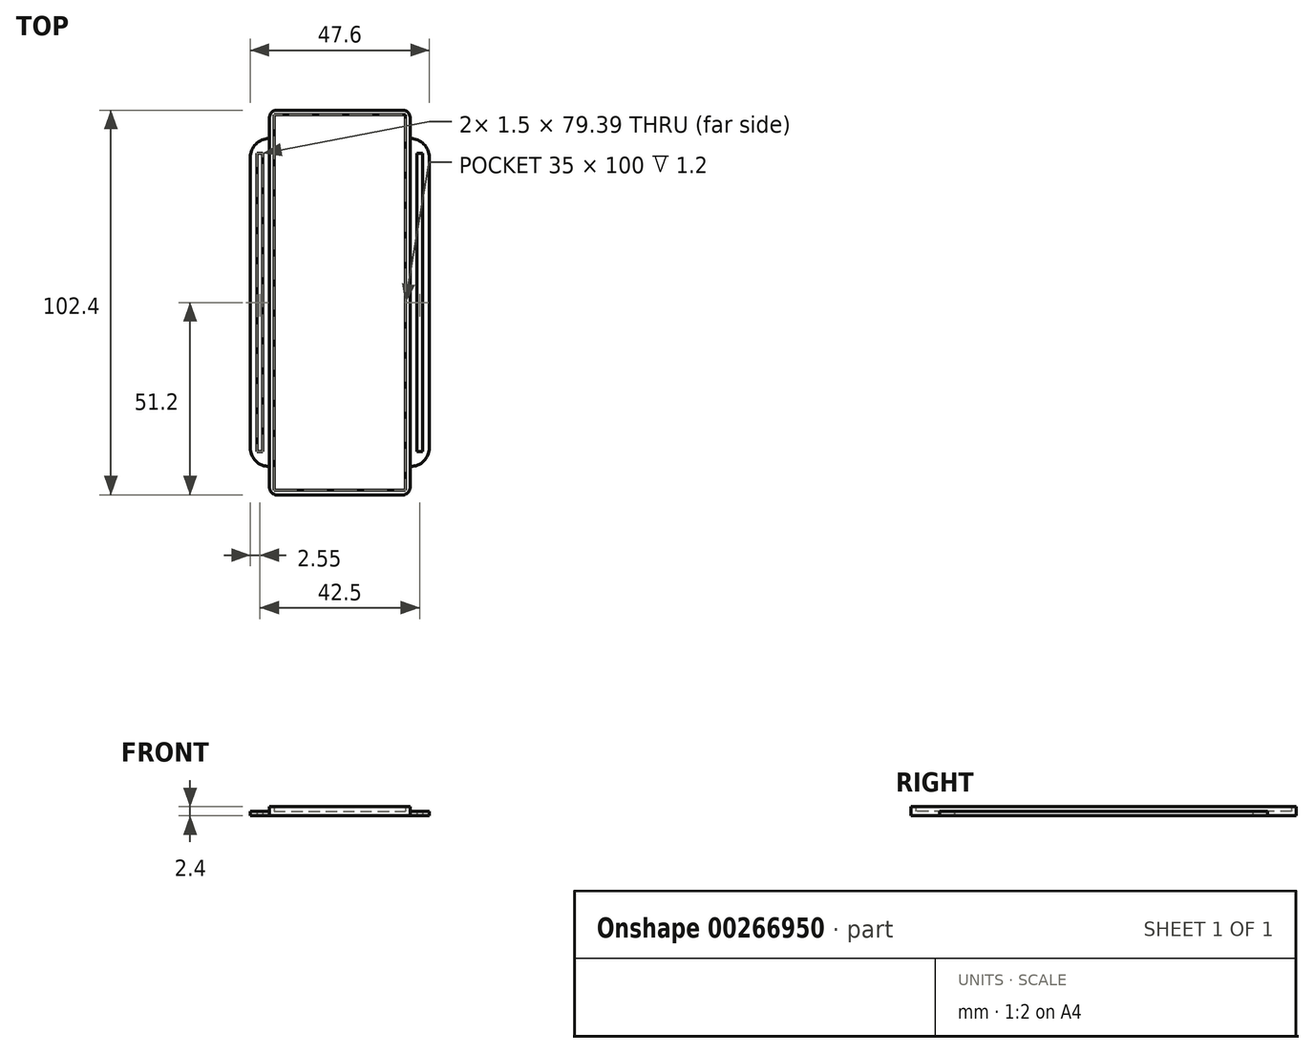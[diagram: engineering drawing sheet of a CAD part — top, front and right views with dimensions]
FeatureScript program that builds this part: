
annotation { "Feature Type Name" : "Feature", "Feature Type Description" : "" }
export const myFeature = defineFeature(function(context is Context, id is Id, definition is map)
    precondition{}
    {
        {
            assignVariable(context, id + "F0", {"name" : "padThickness", "anyValue" : 1.2});
        }
        {
            var Q0;
            Q0=qCreatedBy(makeId("Top.planeOp"),FACE);
            var sketch = newSketch(context, id + "F1", { "sketchPlane" : qUnion([Q0])});
            skLineSegment(sketch, "E0.bottom", {"start": v(-17.5, 50) * mm, "end": v(17.5, 50) * mm});
            skLineSegment(sketch, "E0.top", {"start": v(-17.5, -50) * mm, "end": v(17.5, -50) * mm});
            skLineSegment(sketch, "E0.left", {"start": v(-17.5, 50) * mm, "end": v(-17.5, -50) * mm});
            skLineSegment(sketch, "E0.right", {"start": v(17.5, 50) * mm, "end": v(17.5, -50) * mm});
            skPoint(sketch, "E0.middle", {"position": v(0, 0) * mm});
            skLineSegment(sketch, "E1.0", {"start": v(-18.7, 51.2) * mm, "end": v(18.7, 51.2) * mm});
            skLineSegment(sketch, "E1.1", {"start": v(-18.7, 51.2) * mm, "end": v(-18.7, -51.2) * mm});
            skLineSegment(sketch, "E1.2", {"start": v(-18.7, -51.2) * mm, "end": v(18.7, -51.2) * mm});
            skLineSegment(sketch, "E1.3", {"start": v(18.7, 51.2) * mm, "end": v(18.7, -51.2) * mm});
            skSolve(sketch);
        }
        {
            var Q0;
            Q0=makeQuery(id+"F1.imprint","IMPRINT",FACE,{"disambiguationData":[TD([[makeQuery(id+"F1.imprint","IMPRINT",EDGE,{"derivedFrom":sQuery(id+"F1.wireOp",EDGE,"E0.bottom")}),-1.0]])]});
            extrude(context, id + "F2", {"entities" : qUnion([Q0]), "depth" : (getVariable(context, 'padThickness')) * mm});
        }
        {
            var Q0;
            Q0=makeQuery(id+"F1.imprint","IMPRINT",FACE,{"disambiguationData":[TD([[makeQuery(id+"F1.imprint","IMPRINT",EDGE,{"derivedFrom":sQuery(id+"F1.wireOp",EDGE,"E0.bottom")}),1.0]])]});
            extrude(context, id + "F3", {"entities" : qUnion([Q0]), "operationType" : NewBodyOperationType.ADD, "depth" : (getVariable(context, 'padThickness') * 2) * mm});
        }
        {
            var Q0;
            Q0=makeQuery(id+"F3.opExtrude","SWEPT_EDGE",EDGE,{"disambiguationData":[OSD([sQuery(id+"F1.wireOp",EDGE,"E1.1"),sQuery(id+"F1.wireOp",EDGE,"E1.2")])]});
            var Q1;
            Q1=makeQuery(id+"F3.opExtrude","SWEPT_EDGE",EDGE,{"disambiguationData":[OSD([sQuery(id+"F1.wireOp",EDGE,"E1.2"),sQuery(id+"F1.wireOp",EDGE,"E1.3")])]});
            var Q2;
            Q2=makeQuery(id+"F3.opExtrude","SWEPT_EDGE",EDGE,{"disambiguationData":[OSD([sQuery(id+"F1.wireOp",EDGE,"E1.0"),sQuery(id+"F1.wireOp",EDGE,"E1.3")])]});
            var Q3;
            Q3=makeQuery(id+"F3.opExtrude","SWEPT_EDGE",EDGE,{"disambiguationData":[OSD([sQuery(id+"F1.wireOp",EDGE,"E1.0"),sQuery(id+"F1.wireOp",EDGE,"E1.1")])]});
            fillet(context, id + "F4", {"entities" : qUnion([Q0, Q1, Q2, Q3]), "radius" : 2 * mm, "tangentPropagation" : true, "allowEdgeOverflow" : false});
        }
        {
            var Q0;
            Q0=makeQuery(id+"F1.imprint","IMPRINT",FACE,{"disambiguationData":[TD([[makeQuery(id+"F1.imprint","IMPRINT",EDGE,{"derivedFrom":sQuery(id+"F1.wireOp",EDGE,"E0.bottom")}),-1.0]])]});
            var sketch = newSketch(context, id + "F5", { "sketchPlane" : qUnion([Q0])});
            skLineSegment(sketch, "E2", {"start": v(-18.7, -43.64) * mm, "end": v(-23.8, -43.64) * mm});
            skLineSegment(sketch, "E3", {"start": v(-23.8, -43.64) * mm, "end": v(-23.8, 43.64) * mm});
            skLineSegment(sketch, "E4", {"start": v(-23.8, 43.64) * mm, "end": v(-18.7, 43.64) * mm});
            skPoint(sketch, "E5", {"position": v(-23.8, 0) * mm});
            skLineSegment(sketch, "E6", {"start": v(-23.8, 0) * mm, "end": v(-23.8, -43.64) * mm});
            skLineSegment(sketch, "E7", {"start": v(-23.8, 0) * mm, "end": v(-23.8, 43.64) * mm});
            skLineSegment(sketch, "E8.bottom", {"start": v(-22, -39.7) * mm, "end": v(-20.5, -39.7) * mm});
            skLineSegment(sketch, "E8.top", {"start": v(-22, 39.7) * mm, "end": v(-20.5, 39.7) * mm});
            skLineSegment(sketch, "E8.left", {"start": v(-22, -39.7) * mm, "end": v(-22, 39.7) * mm});
            skLineSegment(sketch, "E8.right", {"start": v(-20.5, -39.7) * mm, "end": v(-20.5, 39.7) * mm});
            skPoint(sketch, "E8.middle", {"position": v(-21.25, 0) * mm});
            skLineSegment(sketch, "E9.MirrorCS", {"start": v(22, -39.7) * mm, "end": v(22, 39.7) * mm});
            skLineSegment(sketch, "E10.MirrorCS", {"start": v(23.8, 0) * mm, "end": v(23.8, -43.64) * mm});
            skLineSegment(sketch, "E11.MirrorCS", {"start": v(18.7, -43.64) * mm, "end": v(23.8, -43.64) * mm});
            skLineSegment(sketch, "E12.MirrorCS", {"start": v(20.5, -39.7) * mm, "end": v(20.5, 39.7) * mm});
            skLineSegment(sketch, "E13.MirrorCS", {"start": v(22, 39.7) * mm, "end": v(20.5, 39.7) * mm});
            skLineSegment(sketch, "E14.MirrorCS", {"start": v(23.8, 43.64) * mm, "end": v(18.7, 43.64) * mm});
            skLineSegment(sketch, "E15.MirrorCS", {"start": v(23.8, 0) * mm, "end": v(23.8, 43.64) * mm});
            skLineSegment(sketch, "E16", {"start": v(-18.7, -43.64) * mm, "end": v(-18.7, 43.64) * mm});
            skLineSegment(sketch, "E17", {"start": v(18.7, 43.64) * mm, "end": v(18.7, -43.64) * mm});
            skLineSegment(sketch, "E18", {"start": v(22, -39.7) * mm, "end": v(20.5, -39.7) * mm});
            skSolve(sketch);
        }
        {
            var Q0;
            Q0=makeQuery(id+"F5.imprint","IMPRINT",FACE,{"disambiguationData":[TD([[makeQuery(id+"F5.imprint","IMPRINT",EDGE,{"derivedFrom":sQuery(id+"F5.wireOp",EDGE,"E2")}),-1.0]])]});
            var Q1;
            Q1=makeQuery(id+"F5.imprint","IMPRINT",FACE,{"disambiguationData":[TD([[makeQuery(id+"F5.imprint","IMPRINT",EDGE,{"derivedFrom":sQuery(id+"F5.wireOp",EDGE,"E9.MirrorCS")}),-1.0]])]});
            extrude(context, id + "F6", {"entities" : qUnion([Q0, Q1]), "operationType" : NewBodyOperationType.ADD, "depth" : (getVariable(context, 'padThickness')) * mm});
        }
        {
            var Q0;
            Q0=makeQuery(id+"F6.opExtrude","SWEPT_EDGE",EDGE,{"disambiguationData":[OSD([sQuery(id+"F5.wireOp",EDGE,"E4"),sQuery(id+"F5.wireOp",EDGE,"E7")])]});
            var Q1;
            Q1=makeQuery(id+"F6.opExtrude","SWEPT_EDGE",EDGE,{"disambiguationData":[OSD([sQuery(id+"F5.wireOp",EDGE,"E14.MirrorCS"),sQuery(id+"F5.wireOp",EDGE,"E15.MirrorCS")])]});
            var Q2;
            Q2=makeQuery(id+"F6.opExtrude","SWEPT_EDGE",EDGE,{"disambiguationData":[OSD([sQuery(id+"F5.wireOp",EDGE,"E10.MirrorCS"),sQuery(id+"F5.wireOp",EDGE,"E11.MirrorCS")])]});
            var Q3;
            Q3=makeQuery(id+"F6.opExtrude","SWEPT_EDGE",EDGE,{"disambiguationData":[OSD([sQuery(id+"F5.wireOp",EDGE,"E2"),sQuery(id+"F5.wireOp",EDGE,"E6")])]});
            fillet(context, id + "F7", {"entities" : qUnion([Q0, Q1, Q2, Q3]), "radius" : 5 * mm, "tangentPropagation" : true, "allowEdgeOverflow" : false});
        }
    });
